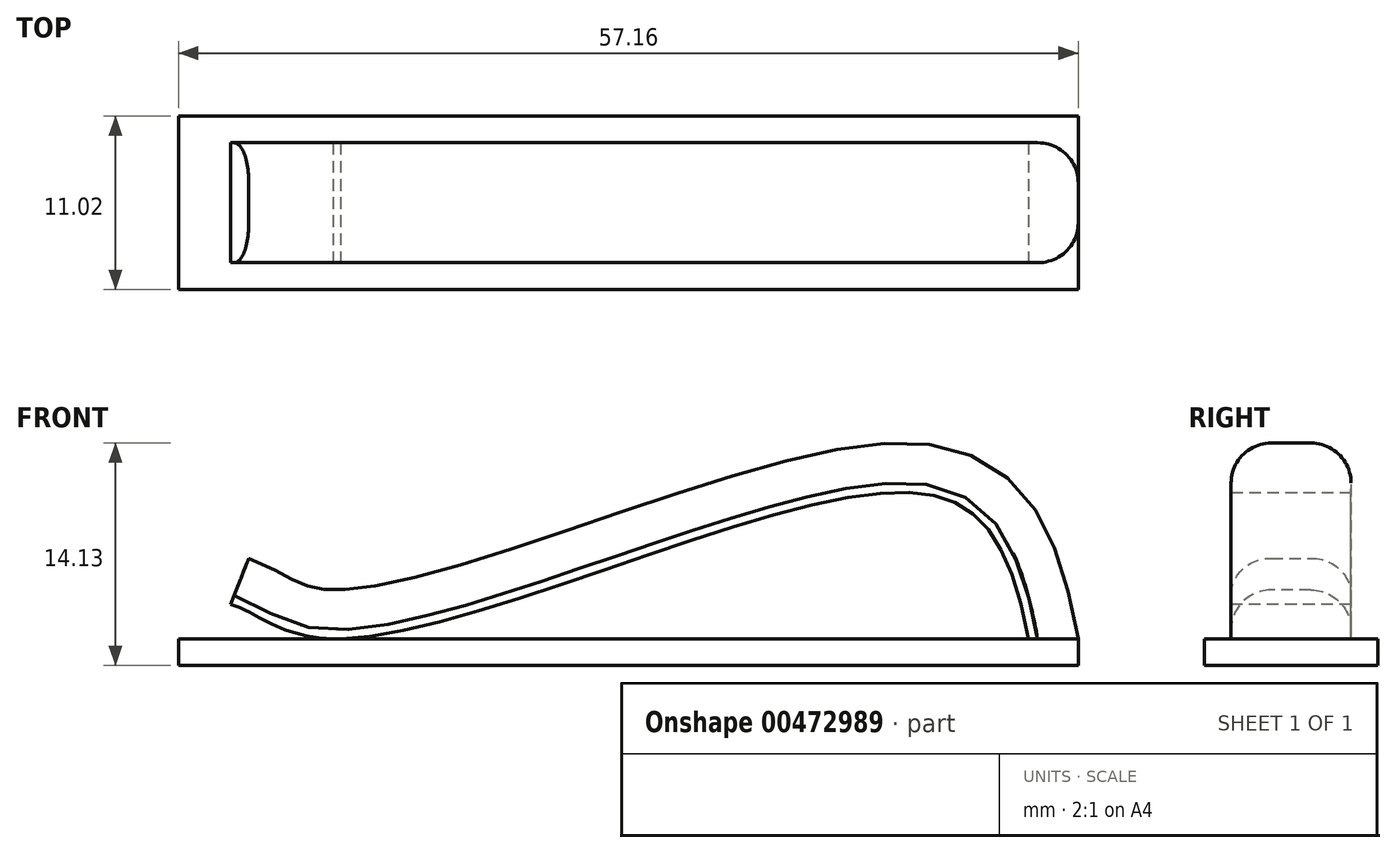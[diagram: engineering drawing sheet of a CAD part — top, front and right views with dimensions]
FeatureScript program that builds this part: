
annotation { "Feature Type Name" : "Feature", "Feature Type Description" : "" }
export const myFeature = defineFeature(function(context is Context, id is Id, definition is map)
    precondition{}
    {
        {
            var Q0;
            Q0=qCreatedBy(makeId("Front.planeOp"),FACE);
            var sketch = newSketch(context, id + "F0", { "sketchPlane" : qUnion([Q0])});
            skLineSegment(sketch, "E0", {"start": v(0, 0) * mm, "end": v(25.4, 0) * mm});
            skLineSegment(sketch, "E1", {"start": v(0, 0) * mm, "end": v(-25.4, 0) * mm});
            skLineSegment(sketch, "E2", {"start": v(25.4, 0) * mm, "end": v(25.4, 1.7) * mm});
            skLineSegment(sketch, "E3.bottom", {"start": v(-18.77, 1.7) * mm, "end": v(-18.77, 1.7) * mm});
            skLineSegment(sketch, "E3.top", {"start": v(16.7, 10.99) * mm, "end": v(16.7, 10.99) * mm});
            skFitSpline(sketch, "E4", {"points": [v(25.4, 1.7) * mm, v(16.7, 10.99) * mm, v(-18.77, 1.7) * mm, v(-25.27, 3.86) * mm], "startDerivative": vector(-13.03, 69.79) * mm, "endDerivative": vector(-20.22, 3.94) * mm});
            skSolve(sketch);
        }
        {
            var Q0;
            Q0=qCreatedBy(makeId("Top.planeOp"),FACE);
            cPlane(context, id + "F1", {"entities" : qUnion([Q0]), "cplaneType" : CPlaneType.OFFSET, "offset" : 1.7 * mm, "width" : 152.4 * mm, "height" : 152.4 * mm});
        }
        {
            var Q0;
            Q0=qCreatedBy(id+"F1.planeOp",FACE);
            var sketch = newSketch(context, id + "F2", { "sketchPlane" : qUnion([Q0])});
            skLineSegment(sketch, "E5", {"start": v(0, 0) * mm, "end": v(25.4, 0) * mm});
            skLineSegment(sketch, "E6", {"start": v(25.4, 0) * mm, "end": v(25.4, -3.8) * mm});
            skLineSegment(sketch, "E7", {"start": v(25.4, -3.8) * mm, "end": v(28.58, -3.8) * mm});
            skLineSegment(sketch, "E8", {"start": v(28.58, -3.8) * mm, "end": v(28.58, 3.81) * mm});
            skLineSegment(sketch, "E9", {"start": v(28.58, 3.81) * mm, "end": v(25.4, 3.81) * mm});
            skLineSegment(sketch, "E10", {"start": v(25.4, 3.81) * mm, "end": v(25.4, 0) * mm});
            skSolve(sketch);
        }
        {
            var Q0;
            Q0=makeQuery(id+"F2.imprint","IMPRINT",FACE,{"disambiguationData":[TD([[makeQuery(id+"F2.imprint","IMPRINT",EDGE,{"derivedFrom":sQuery(id+"F2.wireOp",EDGE,"E6")}),1.0]])]});
            var Q1;
            Q1=sQuery(id+"F0.wireOp",EDGE,"E4");
            sweep(context, id + "F3", {"profiles" : qUnion([Q0]), "path" : qUnion([Q1])});
        }
        {
            var Q0;
            Q0=makeQuery(id+"F3.opSweep","CAP_FACE",FACE,{"disambiguationData":[OSD([sQuery(id+"F0.wireOp",VERTEX,"E4.start"),sQuery(id+"F2.wireOp",EDGE,"E6"),sQuery(id+"F2.wireOp",EDGE,"E7"),sQuery(id+"F2.wireOp",EDGE,"E8"),sQuery(id+"F2.wireOp",EDGE,"E9"),sQuery(id+"F2.wireOp",EDGE,"E10")])],"isStart":true});
            var sketch = newSketch(context, id + "F4", { "sketchPlane" : qUnion([Q0])});
            skLineSegment(sketch, "E11.bottom", {"start": v(28.57, 3.8) * mm, "end": v(-28.57, 3.8) * mm});
            skLineSegment(sketch, "E11.top", {"start": v(28.58, -3.81) * mm, "end": v(-28.58, -3.81) * mm});
            skLineSegment(sketch, "E11.left", {"start": v(28.58, 3.8) * mm, "end": v(28.58, -3.81) * mm});
            skLineSegment(sketch, "E11.right", {"start": v(-28.58, 3.8) * mm, "end": v(-28.58, -3.81) * mm});
            skLineSegment(sketch, "E12.top", {"start": v(28.58, -5.51) * mm, "end": v(-28.58, -5.51) * mm});
            skLineSegment(sketch, "E12.left", {"start": v(28.58, -3.81) * mm, "end": v(28.58, -5.51) * mm});
            skLineSegment(sketch, "E12.right", {"start": v(-28.58, -3.81) * mm, "end": v(-28.58, -5.51) * mm});
            skLineSegment(sketch, "E13.bottom", {"start": v(28.57, 3.8) * mm, "end": v(-28.58, 3.8) * mm});
            skLineSegment(sketch, "E13.top", {"start": v(28.58, 5.51) * mm, "end": v(-28.58, 5.51) * mm});
            skLineSegment(sketch, "E13.left", {"start": v(28.57, 3.8) * mm, "end": v(28.57, 5.51) * mm});
            skLineSegment(sketch, "E13.right", {"start": v(-28.58, 3.8) * mm, "end": v(-28.58, 5.51) * mm});
            skSolve(sketch);
        }
        {
            var Q0;
            {var subQ2=sQuery(id+"F4.wireOp",EDGE,"E11.right");Q0=makeQuery(id+"F4.imprint","IMPRINT",FACE,{"disambiguationData":[TD([[makeQuery(id+"F4.imprint","IMPRINT",EDGE,{"derivedFrom":subQ2}),1.0]])]});}
            var Q1;
            {var subQ2=sQuery(id+"F4.wireOp",EDGE,"E11.left");Q1=makeQuery(id+"F4.imprint","IMPRINT",FACE,{"disambiguationData":[TD([[makeQuery(id+"F4.imprint","IMPRINT",EDGE,{"derivedFrom":subQ2}),-1.0]])]});}
            extrude(context, id + "F5", {"entities" : qUnion([Q0, Q1]), "operationType" : NewBodyOperationType.ADD, "depth" : 1.7 * mm});
        }
        {
            var Q0;
            Q0=makeQuery(id+"F4.imprint","IMPRINT",FACE,{"disambiguationData":[TD([[makeQuery(id+"F4.imprint","IMPRINT",EDGE,{"derivedFrom":sQuery(id+"F4.wireOp",EDGE,"E13.top")}),1.0]])]});
            var Q1;
            Q1=makeQuery(id+"F4.imprint","IMPRINT",FACE,{"disambiguationData":[TD([[makeQuery(id+"F4.imprint","IMPRINT",EDGE,{"derivedFrom":sQuery(id+"F4.wireOp",EDGE,"E12.top")}),-1.0]])]});
            extrude(context, id + "F6", {"entities" : qUnion([Q0, Q1]), "operationType" : NewBodyOperationType.ADD, "depth" : 1.7 * mm});
        }
        {
            var Q0;
            Q0=makeQuery(id+"F3.opSweep","SWEPT_EDGE",EDGE,{"disambiguationData":[OSD([sQuery(id+"F0.wireOp",EDGE,"E4"),sQuery(id+"F2.wireOp",EDGE,"E7"),sQuery(id+"F2.wireOp",EDGE,"E8")])]});
            var Q1;
            Q1=makeQuery(id+"F3.opSweep","SWEPT_EDGE",EDGE,{"disambiguationData":[OSD([sQuery(id+"F0.wireOp",EDGE,"E4"),sQuery(id+"F2.wireOp",EDGE,"E8"),sQuery(id+"F2.wireOp",EDGE,"E9")])]});
            fillet(context, id + "F7", {"entities" : qUnion([Q0, Q1]), "radius" : 2.54 * mm, "tangentPropagation" : true, "allowEdgeOverflow" : false});
        }
    });
